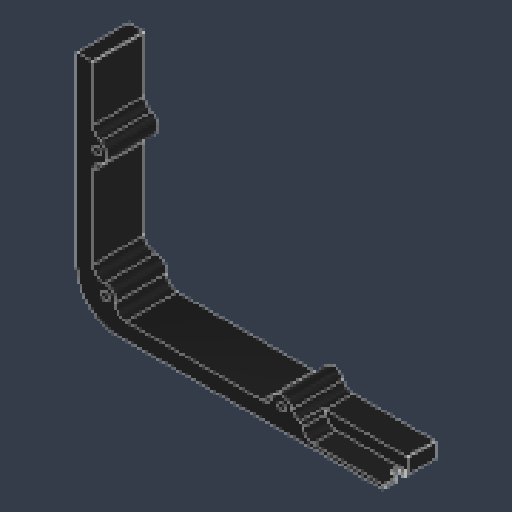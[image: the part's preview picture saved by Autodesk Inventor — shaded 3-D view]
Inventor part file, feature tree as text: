
AUTODESK INVENTOR PART (.ipt)
format: ipt  version: 2023.4 (Build 274418000, 418)  size: 215,040 bytes
history: native  units: mm
features: fillet x8, sketch x5, extrude x4, hole x1
ambient origin geometry x8: Origin, YZ Plane, XZ Plane, XY Plane, X Axis, Y Axis, Z Axis, Center Point
bodies: Solid1 (feature_tree)
feature tree (18):
  extrude  "Extrusion1"  Depth=109.6mm
  fillet  "Fillet1"  Radius=8.0mm
  fillet  "Fillet2"  Radius=8.0mm
  extrude  "Extrusion2"  Depth=25.0mm
  hole  "Hole1"  [1 undecoded]
  fillet  "Fillet3"  Radius=10.0mm
  fillet  "Fillet4"  Radius=14.0mm
  extrude  "Extrusion3"  Depth=73.0mm
  extrude  "Extrusion4"  Depth=10.0mm
  fillet  "Fillet5"  Radius=25.0mm
  fillet  "Fillet6"  Radius=5.0mm
  fillet  "Fillet7"  Radius=0.4mm
  fillet  "Fillet8"  Radius=110.0mm
  sketch  "Sketch1"  dims[d0=149.6mm d1=109.6mm d2=8.0mm d3=8.0mm]
  sketch  "Sketch2"  dims[d4=25.0mm d5=0.0mm d6=12.0mm]
  sketch  "Sketch3"  dims[d7=20.0mm d8=10.0mm d9=10.0mm d10=14.0mm]
  sketch  "Sketch4"  dims[d11=14.0mm d12=73.0mm]
  sketch  "Sketch5"  dims[d13=100.0mm d14=10.0mm d15=25.0mm d16=0.0mm d17=4.0mm d18=6.0mm d19=7.5mm d20=2.0mm d21=90.0deg d22=15.0mm d23=0.0mm d24=5.0mm d25=0.4mm d26=110.0mm d27=13.6mm d29=6.0mm d30=0.0mm d31=0.4mm d32=3.2mm d33=16.6mm d35=9.2mm d36=0.0mm d37=0.0mm d38=0.4mm d39=0.4mm d40=2.0mm d41=5.0mm]
note: 1 required parameter value undecoded (feature->parameter linkage not recoverable at this tier; creation-order binding heuristic only, values carry confidence <= 0.55)
